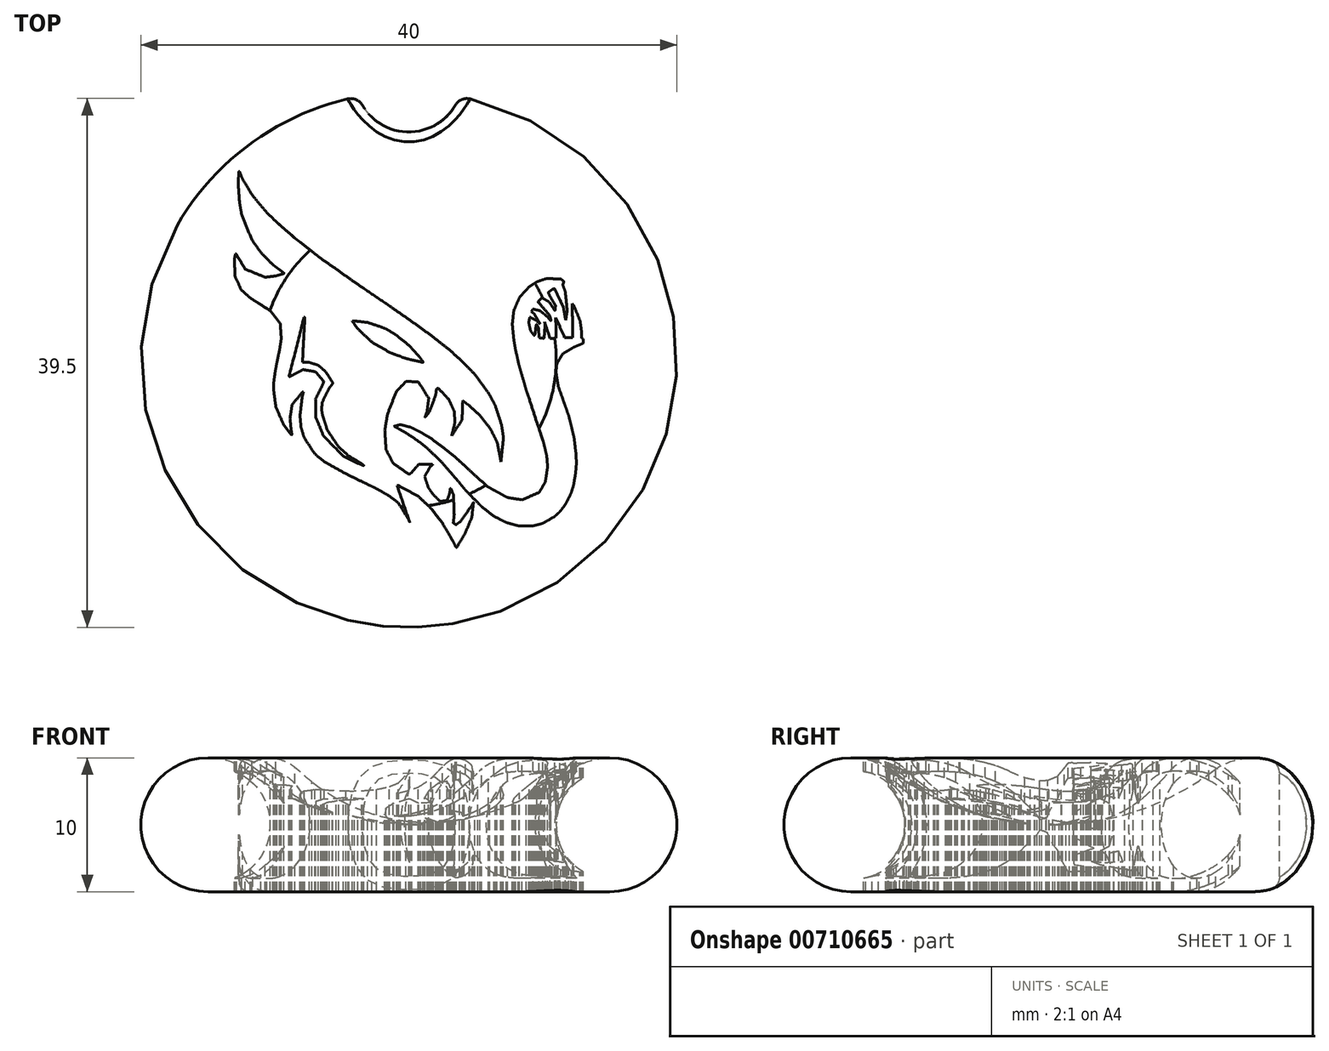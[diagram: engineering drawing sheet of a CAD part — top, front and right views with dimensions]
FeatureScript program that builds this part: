
annotation { "Feature Type Name" : "Feature", "Feature Type Description" : "" }
export const myFeature = defineFeature(function(context is Context, id is Id, definition is map)
    precondition{}
    {
        {
            var Q0;
            Q0=qCreatedBy(makeId("Front.planeOp"),FACE);
            var sketch = newSketch(context, id + "F0", { "sketchPlane" : qUnion([Q0])});
            skArc(sketch, "E0", {"start": v(-12, 9) * mm, "mid": v(-19.74, 6.58) * mm, "end": v(-15, 0) * mm});
            skLineSegment(sketch, "E1", {"start": v(0, 0) * mm, "end": v(-15, 0) * mm});
            skArc(sketch, "E2", {"start": v(-12, 9) * mm, "mid": v(-6.32, 6.03) * mm, "end": v(0, 5) * mm});
            skLineSegment(sketch, "E3", {"start": v(0, 0) * mm, "end": v(0, 5) * mm});
            skSolve(sketch);
        }
        {
            var Q0;
            Q0=makeQuery(id+"F0.imprint","IMPRINT",FACE,{"disambiguationData":[TD([[makeQuery(id+"F0.imprint","IMPRINT",EDGE,{"derivedFrom":sQuery(id+"F0.wireOp",EDGE,"E0")}),1.0]])]});
            var Q1;
            Q1=sQuery(id+"F0.wireOp",EDGE,"E3");
            revolve(context, id + "F1", {"surfaceOperationType" : NewSurfaceOperationType.NEW, "entities" : qUnion([Q0]), "axis" : qUnion([Q1]), "revolveType" : RevolveType.FULL});
        }
        {
            var Q0;
            Q0=qCreatedBy(makeId("Top.planeOp"),FACE);
            cPlane(context, id + "F2", {"entities" : qUnion([Q0]), "cplaneType" : CPlaneType.OFFSET, "offset" : 25 * mm, "width" : 150 * mm, "height" : 150 * mm});
        }
        {
            var Q0;
            Q0=qCreatedBy(id+"F2.planeOp",FACE);
            var sketch = newSketch(context, id + "F3", { "sketchPlane" : qUnion([Q0])});
            skLineSegment(sketch, "E4", {"start": v(0.07, -12.18) * mm, "end": v(-0.88, -9.42) * mm});
            skLineSegment(sketch, "E5", {"start": v(-0.88, -9.42) * mm, "end": v(-0.75, -9.42) * mm});
            skLineSegment(sketch, "E6", {"start": v(-0.75, -9.42) * mm, "end": v(0.69, -10.2) * mm});
            skLineSegment(sketch, "E7", {"start": v(0.69, -10.2) * mm, "end": v(1.64, -11.1) * mm});
            skLineSegment(sketch, "E8", {"start": v(1.64, -11.1) * mm, "end": v(2.5, -12.21) * mm});
            skLineSegment(sketch, "E9", {"start": v(2.5, -12.21) * mm, "end": v(3.22, -13.43) * mm});
            skLineSegment(sketch, "E10", {"start": v(3.22, -13.43) * mm, "end": v(3.46, -13.9) * mm});
            skLineSegment(sketch, "E11", {"start": v(3.46, -13.9) * mm, "end": v(3.55, -14.05) * mm});
            skLineSegment(sketch, "E12", {"start": v(3.55, -14.05) * mm, "end": v(4.21, -12.95) * mm});
            skLineSegment(sketch, "E13", {"start": v(4.21, -12.95) * mm, "end": v(4.7, -11.8) * mm});
            skLineSegment(sketch, "E14", {"start": v(4.7, -11.8) * mm, "end": v(4.82, -10.65) * mm});
            skLineSegment(sketch, "E15", {"start": v(4.82, -10.65) * mm, "end": v(4.73, -10.86) * mm});
            skLineSegment(sketch, "E16", {"start": v(4.73, -10.86) * mm, "end": v(3.84, -12.1) * mm});
            skLineSegment(sketch, "E17", {"start": v(3.84, -12.1) * mm, "end": v(3.52, -12.34) * mm});
            skLineSegment(sketch, "E18", {"start": v(3.52, -12.34) * mm, "end": v(3.31, -12.2) * mm});
            skLineSegment(sketch, "E19", {"start": v(3.31, -12.2) * mm, "end": v(3.39, -11.6) * mm});
            skLineSegment(sketch, "E20", {"start": v(3.39, -11.6) * mm, "end": v(3.33, -10.1) * mm});
            skLineSegment(sketch, "E21", {"start": v(3.33, -10.1) * mm, "end": v(3.14, -9.62) * mm});
            skLineSegment(sketch, "E22", {"start": v(3.14, -9.62) * mm, "end": v(3.1, -9.63) * mm});
            skLineSegment(sketch, "E23", {"start": v(3.1, -9.63) * mm, "end": v(3.03, -10.02) * mm});
            skLineSegment(sketch, "E24", {"start": v(3.03, -10.02) * mm, "end": v(2.86, -10.52) * mm});
            skLineSegment(sketch, "E25", {"start": v(2.86, -10.52) * mm, "end": v(2.33, -10.6) * mm});
            skLineSegment(sketch, "E26", {"start": v(2.33, -10.6) * mm, "end": v(1.78, -10.04) * mm});
            skLineSegment(sketch, "E27", {"start": v(1.78, -10.04) * mm, "end": v(1.45, -9.56) * mm});
            skLineSegment(sketch, "E28", {"start": v(1.45, -9.56) * mm, "end": v(1.18, -8.73) * mm});
            skLineSegment(sketch, "E29", {"start": v(1.18, -8.73) * mm, "end": v(1.63, -7.94) * mm});
            skLineSegment(sketch, "E30", {"start": v(1.63, -7.94) * mm, "end": v(1.79, -7.87) * mm});
            skLineSegment(sketch, "E31", {"start": v(1.79, -7.87) * mm, "end": v(1.68, -7.8) * mm});
            skLineSegment(sketch, "E32", {"start": v(1.68, -7.8) * mm, "end": v(0.73, -7.82) * mm});
            skLineSegment(sketch, "E33", {"start": v(0.73, -7.82) * mm, "end": v(0.17, -8.48) * mm});
            skLineSegment(sketch, "E34", {"start": v(0.17, -8.48) * mm, "end": v(0, -8.57) * mm});
            skLineSegment(sketch, "E35", {"start": v(0, -8.57) * mm, "end": v(-1.18, -7.73) * mm});
            skLineSegment(sketch, "E36", {"start": v(-1.18, -7.73) * mm, "end": v(-1.7, -6.73) * mm});
            skLineSegment(sketch, "E37", {"start": v(-1.7, -6.73) * mm, "end": v(-1.8, -5.27) * mm});
            skLineSegment(sketch, "E38", {"start": v(-1.8, -5.27) * mm, "end": v(-1.6, -4.06) * mm});
            skLineSegment(sketch, "E39", {"start": v(-1.6, -4.06) * mm, "end": v(-0.93, -2.38) * mm});
            skLineSegment(sketch, "E40", {"start": v(-0.93, -2.38) * mm, "end": v(-0.2, -1.64) * mm});
            skLineSegment(sketch, "E41", {"start": v(-0.2, -1.64) * mm, "end": v(0.7, -1.65) * mm});
            skLineSegment(sketch, "E42", {"start": v(0.7, -1.65) * mm, "end": v(1.48, -2.9) * mm});
            skLineSegment(sketch, "E43", {"start": v(1.48, -2.9) * mm, "end": v(1.36, -3.87) * mm});
            skLineSegment(sketch, "E44", {"start": v(1.36, -3.87) * mm, "end": v(1.2, -4.32) * mm});
            skLineSegment(sketch, "E45", {"start": v(1.2, -4.32) * mm, "end": v(1.55, -3.88) * mm});
            skLineSegment(sketch, "E46", {"start": v(1.55, -3.88) * mm, "end": v(2, -2.65) * mm});
            skLineSegment(sketch, "E47", {"start": v(2, -2.65) * mm, "end": v(2.07, -2.19) * mm});
            skLineSegment(sketch, "E48", {"start": v(2.07, -2.19) * mm, "end": v(2.2, -2.14) * mm});
            skLineSegment(sketch, "E49", {"start": v(2.2, -2.14) * mm, "end": v(2.97, -2.96) * mm});
            skLineSegment(sketch, "E50", {"start": v(2.97, -2.96) * mm, "end": v(3.39, -3.87) * mm});
            skLineSegment(sketch, "E51", {"start": v(3.39, -3.87) * mm, "end": v(3.44, -4.7) * mm});
            skLineSegment(sketch, "E52", {"start": v(3.44, -4.7) * mm, "end": v(3.22, -5.56) * mm});
            skLineSegment(sketch, "E53", {"start": v(3.22, -5.56) * mm, "end": v(3.2, -5.7) * mm});
            skLineSegment(sketch, "E54", {"start": v(3.2, -5.7) * mm, "end": v(3.97, -4.5) * mm});
            skLineSegment(sketch, "E55", {"start": v(3.97, -4.5) * mm, "end": v(4.02, -3.07) * mm});
            skLineSegment(sketch, "E56", {"start": v(4.02, -3.07) * mm, "end": v(4.5, -3.42) * mm});
            skLineSegment(sketch, "E57", {"start": v(4.5, -3.42) * mm, "end": v(5.3, -4.17) * mm});
            skLineSegment(sketch, "E58", {"start": v(5.3, -4.17) * mm, "end": v(6.05, -5.1) * mm});
            skLineSegment(sketch, "E59", {"start": v(6.05, -5.1) * mm, "end": v(6.59, -6.16) * mm});
            skLineSegment(sketch, "E60", {"start": v(6.59, -6.16) * mm, "end": v(6.85, -7.5) * mm});
            skLineSegment(sketch, "E61", {"start": v(6.85, -7.5) * mm, "end": v(6.87, -7.64) * mm});
            skLineSegment(sketch, "E62", {"start": v(6.87, -7.64) * mm, "end": v(7.06, -5.83) * mm});
            skLineSegment(sketch, "E63", {"start": v(7.06, -5.83) * mm, "end": v(6.91, -4.86) * mm});
            skLineSegment(sketch, "E64", {"start": v(6.91, -4.86) * mm, "end": v(6.45, -3.44) * mm});
            skLineSegment(sketch, "E65", {"start": v(6.45, -3.44) * mm, "end": v(5.94, -2.5) * mm});
            skLineSegment(sketch, "E66", {"start": v(5.94, -2.5) * mm, "end": v(4.93, -1.11) * mm});
            skLineSegment(sketch, "E67", {"start": v(4.93, -1.11) * mm, "end": v(3.78, 0.06) * mm});
            skLineSegment(sketch, "E68", {"start": v(3.78, 0.06) * mm, "end": v(2.93, 0.8) * mm});
            skLineSegment(sketch, "E69", {"start": v(2.93, 0.8) * mm, "end": v(1.83, 1.66) * mm});
            skLineSegment(sketch, "E70", {"start": v(1.83, 1.66) * mm, "end": v(0.88, 2.38) * mm});
            skLineSegment(sketch, "E71", {"start": v(0.88, 2.38) * mm, "end": v(-0.09, 3.06) * mm});
            skLineSegment(sketch, "E72", {"start": v(-0.09, 3.06) * mm, "end": v(-1.43, 4) * mm});
            skLineSegment(sketch, "E73", {"start": v(-1.43, 4) * mm, "end": v(-3.32, 5.28) * mm});
            skLineSegment(sketch, "E74", {"start": v(-3.32, 5.28) * mm, "end": v(-4.48, 6.08) * mm});
            skLineSegment(sketch, "E75", {"start": v(-4.48, 6.08) * mm, "end": v(-5.43, 6.77) * mm});
            skLineSegment(sketch, "E76", {"start": v(-5.43, 6.77) * mm, "end": v(-6.58, 7.57) * mm});
            skLineSegment(sketch, "E77", {"start": v(-6.58, 7.57) * mm, "end": v(-7.24, 8.07) * mm});
            skLineSegment(sketch, "E78", {"start": v(-7.24, 8.07) * mm, "end": v(-8.5, 9.07) * mm});
            skLineSegment(sketch, "E79", {"start": v(-8.5, 9.07) * mm, "end": v(-9.94, 10.33) * mm});
            skLineSegment(sketch, "E80", {"start": v(-9.94, 10.33) * mm, "end": v(-10.62, 11) * mm});
            skLineSegment(sketch, "E81", {"start": v(-10.62, 11) * mm, "end": v(-11.66, 12.24) * mm});
            skLineSegment(sketch, "E82", {"start": v(-11.66, 12.24) * mm, "end": v(-12.4, 13.46) * mm});
            skLineSegment(sketch, "E83", {"start": v(-12.4, 13.46) * mm, "end": v(-12.64, 14.05) * mm});
            skLineSegment(sketch, "E84", {"start": v(-12.64, 14.05) * mm, "end": v(-12.69, 14.05) * mm});
            skLineSegment(sketch, "E85", {"start": v(-12.69, 14.05) * mm, "end": v(-12.74, 13.18) * mm});
            skLineSegment(sketch, "E86", {"start": v(-12.74, 13.18) * mm, "end": v(-12.64, 11.7) * mm});
            skLineSegment(sketch, "E87", {"start": v(-12.64, 11.7) * mm, "end": v(-12.48, 10.82) * mm});
            skLineSegment(sketch, "E88", {"start": v(-12.48, 10.82) * mm, "end": v(-11.72, 8.95) * mm});
            skLineSegment(sketch, "E89", {"start": v(-11.72, 8.95) * mm, "end": v(-11.06, 8.01) * mm});
            skLineSegment(sketch, "E90", {"start": v(-11.06, 8.01) * mm, "end": v(-10.15, 7.08) * mm});
            skLineSegment(sketch, "E91", {"start": v(-10.15, 7.08) * mm, "end": v(-9.53, 6.62) * mm});
            skLineSegment(sketch, "E92", {"start": v(-9.53, 6.62) * mm, "end": v(-9.33, 6.47) * mm});
            skLineSegment(sketch, "E93", {"start": v(-9.33, 6.47) * mm, "end": v(-9.33, 6.42) * mm});
            skLineSegment(sketch, "E94", {"start": v(-9.33, 6.42) * mm, "end": v(-9.94, 6.25) * mm});
            skLineSegment(sketch, "E95", {"start": v(-9.94, 6.25) * mm, "end": v(-10.73, 6.15) * mm});
            skLineSegment(sketch, "E96", {"start": v(-10.73, 6.15) * mm, "end": v(-12.21, 6.75) * mm});
            skLineSegment(sketch, "E97", {"start": v(-12.21, 6.75) * mm, "end": v(-12.87, 7.83) * mm});
            skLineSegment(sketch, "E98", {"start": v(-12.87, 7.83) * mm, "end": v(-12.9, 7.88) * mm});
            skLineSegment(sketch, "E99", {"start": v(-12.9, 7.88) * mm, "end": v(-12.94, 7.9) * mm});
            skLineSegment(sketch, "E100", {"start": v(-12.94, 7.9) * mm, "end": v(-13.02, 7.52) * mm});
            skLineSegment(sketch, "E101", {"start": v(-13.02, 7.52) * mm, "end": v(-12.98, 6.24) * mm});
            skLineSegment(sketch, "E102", {"start": v(-12.98, 6.24) * mm, "end": v(-12.5, 5.2) * mm});
            skLineSegment(sketch, "E103", {"start": v(-12.5, 5.2) * mm, "end": v(-11.85, 4.61) * mm});
            skLineSegment(sketch, "E104", {"start": v(-11.85, 4.61) * mm, "end": v(-10.35, 3.65) * mm});
            skLineSegment(sketch, "E105", {"start": v(-10.35, 3.65) * mm, "end": v(-9.6, 2.71) * mm});
            skLineSegment(sketch, "E106", {"start": v(-9.6, 2.71) * mm, "end": v(-9.52, 1.56) * mm});
            skLineSegment(sketch, "E107", {"start": v(-9.52, 1.56) * mm, "end": v(-9.66, 0.71) * mm});
            skLineSegment(sketch, "E108", {"start": v(-9.66, 0.71) * mm, "end": v(-9.85, -0.2) * mm});
            skLineSegment(sketch, "E109", {"start": v(-9.85, -0.2) * mm, "end": v(-9.98, -0.93) * mm});
            skLineSegment(sketch, "E110", {"start": v(-9.98, -0.93) * mm, "end": v(-10.08, -1.62) * mm});
            skLineSegment(sketch, "E111", {"start": v(-10.08, -1.62) * mm, "end": v(-10.1, -2.3) * mm});
            skLineSegment(sketch, "E112", {"start": v(-10.1, -2.3) * mm, "end": v(-9.93, -3.55) * mm});
            skLineSegment(sketch, "E113", {"start": v(-9.93, -3.55) * mm, "end": v(-9.33, -4.9) * mm});
            skLineSegment(sketch, "E114", {"start": v(-9.33, -4.9) * mm, "end": v(-8.77, -5.62) * mm});
            skLineSegment(sketch, "E115", {"start": v(-8.77, -5.62) * mm, "end": v(-8.73, -5.6) * mm});
            skLineSegment(sketch, "E116", {"start": v(-8.73, -5.6) * mm, "end": v(-8.78, -5.33) * mm});
            skLineSegment(sketch, "E117", {"start": v(-8.78, -5.33) * mm, "end": v(-8.88, -4.41) * mm});
            skLineSegment(sketch, "E118", {"start": v(-8.88, -4.41) * mm, "end": v(-8.72, -3.39) * mm});
            skLineSegment(sketch, "E119", {"start": v(-8.72, -3.39) * mm, "end": v(-7.97, -2.44) * mm});
            skLineSegment(sketch, "E120", {"start": v(-7.97, -2.44) * mm, "end": v(-7.92, -2.41) * mm});
            skLineSegment(sketch, "E121", {"start": v(-7.92, -2.41) * mm, "end": v(-7.87, -2.41) * mm});
            skLineSegment(sketch, "E122", {"start": v(-7.87, -2.41) * mm, "end": v(-7.96, -2.8) * mm});
            skLineSegment(sketch, "E123", {"start": v(-7.96, -2.8) * mm, "end": v(-8.13, -4.2) * mm});
            skLineSegment(sketch, "E124", {"start": v(-8.13, -4.2) * mm, "end": v(-8.05, -5.05) * mm});
            skLineSegment(sketch, "E125", {"start": v(-8.05, -5.05) * mm, "end": v(-7.82, -5.83) * mm});
            skLineSegment(sketch, "E126", {"start": v(-7.82, -5.83) * mm, "end": v(-7.02, -7.05) * mm});
            skLineSegment(sketch, "E127", {"start": v(-7.02, -7.05) * mm, "end": v(-6.33, -7.62) * mm});
            skLineSegment(sketch, "E128", {"start": v(-6.33, -7.62) * mm, "end": v(-4.7, -8.54) * mm});
            skLineSegment(sketch, "E129", {"start": v(-4.7, -8.54) * mm, "end": v(-3.37, -9.19) * mm});
            skLineSegment(sketch, "E130", {"start": v(-3.37, -9.19) * mm, "end": v(-2.41, -9.64) * mm});
            skLineSegment(sketch, "E131", {"start": v(-2.41, -9.64) * mm, "end": v(-1.47, -10.19) * mm});
            skLineSegment(sketch, "E132", {"start": v(-1.47, -10.19) * mm, "end": v(-0.8, -10.7) * mm});
            skLineSegment(sketch, "E133", {"start": v(-0.8, -10.7) * mm, "end": v(0, -11.97) * mm});
            skLineSegment(sketch, "E134", {"start": v(0, -11.97) * mm, "end": v(0.07, -12.18) * mm});
            skLineSegment(sketch, "E135", {"start": v(-7.94, -0.21) * mm, "end": v(-7.42, -0.22) * mm});
            skLineSegment(sketch, "E136", {"start": v(-7.42, -0.22) * mm, "end": v(-6.76, -0.43) * mm});
            skLineSegment(sketch, "E137", {"start": v(-6.76, -0.43) * mm, "end": v(-6.2, -0.9) * mm});
            skLineSegment(sketch, "E138", {"start": v(-6.2, -0.9) * mm, "end": v(-5.68, -1.73) * mm});
            skLineSegment(sketch, "E139", {"start": v(-5.68, -1.73) * mm, "end": v(-5.7, -1.83) * mm});
            skLineSegment(sketch, "E140", {"start": v(-5.7, -1.83) * mm, "end": v(-5.95, -2.13) * mm});
            skLineSegment(sketch, "E141", {"start": v(-5.95, -2.13) * mm, "end": v(-6.46, -3.17) * mm});
            skLineSegment(sketch, "E142", {"start": v(-6.46, -3.17) * mm, "end": v(-6.52, -3.72) * mm});
            skLineSegment(sketch, "E143", {"start": v(-6.52, -3.72) * mm, "end": v(-6.43, -4.19) * mm});
            skLineSegment(sketch, "E144", {"start": v(-6.43, -4.19) * mm, "end": v(-6.08, -5.28) * mm});
            skLineSegment(sketch, "E145", {"start": v(-6.08, -5.28) * mm, "end": v(-5.24, -6.53) * mm});
            skLineSegment(sketch, "E146", {"start": v(-5.24, -6.53) * mm, "end": v(-4.53, -7.18) * mm});
            skLineSegment(sketch, "E147", {"start": v(-4.53, -7.18) * mm, "end": v(-3.52, -7.78) * mm});
            skLineSegment(sketch, "E148", {"start": v(-3.52, -7.78) * mm, "end": v(-3.35, -7.9) * mm});
            skLineSegment(sketch, "E149", {"start": v(-3.35, -7.9) * mm, "end": v(-3.41, -7.92) * mm});
            skLineSegment(sketch, "E150", {"start": v(-3.41, -7.92) * mm, "end": v(-4.9, -7.23) * mm});
            skLineSegment(sketch, "E151", {"start": v(-4.9, -7.23) * mm, "end": v(-6.38, -5.68) * mm});
            skLineSegment(sketch, "E152", {"start": v(-6.38, -5.68) * mm, "end": v(-6.94, -4.33) * mm});
            skLineSegment(sketch, "E153", {"start": v(-6.94, -4.33) * mm, "end": v(-6.97, -2.96) * mm});
            skLineSegment(sketch, "E154", {"start": v(-6.97, -2.96) * mm, "end": v(-6.4, -1.78) * mm});
            skLineSegment(sketch, "E155", {"start": v(-6.4, -1.78) * mm, "end": v(-6.36, -1.64) * mm});
            skLineSegment(sketch, "E156", {"start": v(-6.36, -1.64) * mm, "end": v(-6.97, -0.9) * mm});
            skLineSegment(sketch, "E157", {"start": v(-6.97, -0.9) * mm, "end": v(-7.9, -0.75) * mm});
            skLineSegment(sketch, "E158", {"start": v(-7.9, -0.75) * mm, "end": v(-8.75, -1.2) * mm});
            skLineSegment(sketch, "E159", {"start": v(-8.75, -1.2) * mm, "end": v(-8.9, -1.28) * mm});
            skLineSegment(sketch, "E160", {"start": v(-8.9, -1.28) * mm, "end": v(-8.94, -1.26) * mm});
            skLineSegment(sketch, "E161", {"start": v(-8.94, -1.26) * mm, "end": v(-7.83, 3.16) * mm});
            skLineSegment(sketch, "E162", {"start": v(-7.83, 3.16) * mm, "end": v(-7.77, 3.15) * mm});
            skLineSegment(sketch, "E163", {"start": v(-7.77, 3.15) * mm, "end": v(-7.94, -0.21) * mm});
            skLineSegment(sketch, "E164", {"start": v(-4.23, 2.88) * mm, "end": v(-4.07, 2.88) * mm});
            skLineSegment(sketch, "E165", {"start": v(-4.07, 2.88) * mm, "end": v(-3.07, 2.77) * mm});
            skLineSegment(sketch, "E166", {"start": v(-3.07, 2.77) * mm, "end": v(-1.78, 2.33) * mm});
            skLineSegment(sketch, "E167", {"start": v(-1.78, 2.33) * mm, "end": v(-0.94, 1.82) * mm});
            skLineSegment(sketch, "E168", {"start": v(-0.94, 1.82) * mm, "end": v(0.03, 1.04) * mm});
            skLineSegment(sketch, "E169", {"start": v(0.03, 1.04) * mm, "end": v(0.77, 0.23) * mm});
            skLineSegment(sketch, "E170", {"start": v(0.77, 0.23) * mm, "end": v(1.07, -0.2) * mm});
            skLineSegment(sketch, "E171", {"start": v(1.07, -0.2) * mm, "end": v(1.06, -0.22) * mm});
            skLineSegment(sketch, "E172", {"start": v(1.06, -0.22) * mm, "end": v(0.89, -0.18) * mm});
            skLineSegment(sketch, "E173", {"start": v(0.89, -0.18) * mm, "end": v(-0.23, 0.08) * mm});
            skLineSegment(sketch, "E174", {"start": v(-0.23, 0.08) * mm, "end": v(-1.43, 0.53) * mm});
            skLineSegment(sketch, "E175", {"start": v(-1.43, 0.53) * mm, "end": v(-2.76, 1.3) * mm});
            skLineSegment(sketch, "E176", {"start": v(-2.76, 1.3) * mm, "end": v(-3.82, 2.3) * mm});
            skLineSegment(sketch, "E177", {"start": v(-3.82, 2.3) * mm, "end": v(-4.23, 2.88) * mm});
            skLineSegment(sketch, "E178", {"start": v(10.06, 1.59) * mm, "end": v(9.72, 1.63) * mm});
            skLineSegment(sketch, "E179", {"start": v(9.35, 1.8) * mm, "end": v(9.08, 2.16) * mm});
            skLineSegment(sketch, "E180", {"start": v(9.08, 2.16) * mm, "end": v(8.95, 2.77) * mm});
            skLineSegment(sketch, "E181", {"start": v(8.95, 2.77) * mm, "end": v(9.03, 3.17) * mm});
            skLineSegment(sketch, "E182", {"start": v(9.15, 3.57) * mm, "end": v(9.25, 3.78) * mm});
            skLineSegment(sketch, "E183", {"start": v(9.64, 4.32) * mm, "end": v(9.93, 4.62) * mm});
            skLineSegment(sketch, "E184", {"start": v(10.38, 5) * mm, "end": v(10.7, 5.24) * mm});
            skLineSegment(sketch, "E185", {"start": v(10.7, 5.24) * mm, "end": v(10.87, 5.3) * mm});
            skLineSegment(sketch, "E186", {"start": v(11.5, 5.6) * mm, "end": v(11.5, 5.63) * mm});
            skLineSegment(sketch, "E187", {"start": v(11.5, 5.63) * mm, "end": v(11.57, 5.84) * mm});
            skLineSegment(sketch, "E188", {"start": v(11.57, 5.84) * mm, "end": v(11.33, 6.02) * mm});
            skLineSegment(sketch, "E189", {"start": v(11.33, 6.02) * mm, "end": v(10.26, 6.05) * mm});
            skLineSegment(sketch, "E190", {"start": v(10.26, 6.05) * mm, "end": v(9.55, 5.8) * mm});
            skLineSegment(sketch, "E191", {"start": v(9.55, 5.8) * mm, "end": v(8.99, 5.44) * mm});
            skLineSegment(sketch, "E192", {"start": v(8.99, 5.44) * mm, "end": v(8.26, 4.65) * mm});
            skLineSegment(sketch, "E193", {"start": v(8.26, 4.65) * mm, "end": v(7.83, 3.67) * mm});
            skLineSegment(sketch, "E194", {"start": v(7.83, 3.67) * mm, "end": v(7.72, 2.64) * mm});
            skLineSegment(sketch, "E195", {"start": v(7.72, 2.64) * mm, "end": v(7.82, 1.57) * mm});
            skLineSegment(sketch, "E196", {"start": v(7.82, 1.57) * mm, "end": v(7.96, 0.75) * mm});
            skLineSegment(sketch, "E197", {"start": v(7.96, 0.75) * mm, "end": v(8.22, -0.4) * mm});
            skLineSegment(sketch, "E198", {"start": v(8.22, -0.4) * mm, "end": v(8.51, -1.41) * mm});
            skLineSegment(sketch, "E199", {"start": v(8.51, -1.41) * mm, "end": v(8.77, -2.3) * mm});
            skLineSegment(sketch, "E200", {"start": v(8.77, -2.3) * mm, "end": v(8.95, -2.83) * mm});
            skLineSegment(sketch, "E201", {"start": v(8.95, -2.83) * mm, "end": v(9.55, -4.7) * mm});
            skLineSegment(sketch, "E202", {"start": v(9.55, -4.7) * mm, "end": v(10.03, -6.12) * mm});
            skLineSegment(sketch, "E203", {"start": v(10.03, -6.12) * mm, "end": v(10.3, -7.18) * mm});
            skLineSegment(sketch, "E204", {"start": v(10.3, -7.18) * mm, "end": v(10.36, -8.03) * mm});
            skLineSegment(sketch, "E205", {"start": v(10.36, -8.03) * mm, "end": v(10.18, -9.16) * mm});
            skLineSegment(sketch, "E206", {"start": v(10.18, -9.16) * mm, "end": v(9.73, -9.92) * mm});
            skLineSegment(sketch, "E207", {"start": v(9.73, -9.92) * mm, "end": v(8.46, -10.48) * mm});
            skLineSegment(sketch, "E208", {"start": v(8.46, -10.48) * mm, "end": v(7.35, -10.3) * mm});
            skLineSegment(sketch, "E209", {"start": v(7.35, -10.3) * mm, "end": v(5.93, -9.52) * mm});
            skLineSegment(sketch, "E210", {"start": v(5.93, -9.52) * mm, "end": v(5.13, -8.83) * mm});
            skLineSegment(sketch, "E211", {"start": v(5.13, -8.83) * mm, "end": v(4.04, -7.8) * mm});
            skLineSegment(sketch, "E212", {"start": v(4.04, -7.8) * mm, "end": v(3.4, -7.23) * mm});
            skLineSegment(sketch, "E213", {"start": v(3.4, -7.23) * mm, "end": v(2.59, -6.59) * mm});
            skLineSegment(sketch, "E214", {"start": v(2.59, -6.59) * mm, "end": v(1.57, -5.83) * mm});
            skLineSegment(sketch, "E215", {"start": v(1.57, -5.83) * mm, "end": v(0.83, -5.4) * mm});
            skLineSegment(sketch, "E216", {"start": v(0.83, -5.4) * mm, "end": v(0.12, -5.05) * mm});
            skLineSegment(sketch, "E217", {"start": v(0.12, -5.05) * mm, "end": v(-0.64, -4.85) * mm});
            skLineSegment(sketch, "E218", {"start": v(-0.64, -4.85) * mm, "end": v(-1.1, -4.99) * mm});
            skLineSegment(sketch, "E219", {"start": v(-1.1, -4.99) * mm, "end": v(-0.72, -5.18) * mm});
            skLineSegment(sketch, "E220", {"start": v(-0.72, -5.18) * mm, "end": v(0.22, -5.75) * mm});
            skLineSegment(sketch, "E221", {"start": v(0.22, -5.75) * mm, "end": v(0.85, -6.2) * mm});
            skLineSegment(sketch, "E222", {"start": v(0.85, -6.2) * mm, "end": v(1.45, -6.7) * mm});
            skLineSegment(sketch, "E223", {"start": v(1.45, -6.7) * mm, "end": v(2.43, -7.64) * mm});
            skLineSegment(sketch, "E224", {"start": v(2.43, -7.64) * mm, "end": v(3.27, -8.62) * mm});
            skLineSegment(sketch, "E225", {"start": v(3.27, -8.62) * mm, "end": v(3.76, -9.19) * mm});
            skLineSegment(sketch, "E226", {"start": v(3.76, -9.19) * mm, "end": v(4.11, -9.63) * mm});
            skLineSegment(sketch, "E227", {"start": v(4.11, -9.63) * mm, "end": v(4.54, -10.08) * mm});
            skLineSegment(sketch, "E228", {"start": v(4.54, -10.08) * mm, "end": v(5.44, -11) * mm});
            skLineSegment(sketch, "E229", {"start": v(5.44, -11) * mm, "end": v(6.34, -11.7) * mm});
            skLineSegment(sketch, "E230", {"start": v(6.34, -11.7) * mm, "end": v(7.27, -12.17) * mm});
            skLineSegment(sketch, "E231", {"start": v(7.27, -12.17) * mm, "end": v(8.15, -12.42) * mm});
            skLineSegment(sketch, "E232", {"start": v(8.15, -12.42) * mm, "end": v(9.26, -12.42) * mm});
            skLineSegment(sketch, "E233", {"start": v(9.26, -12.42) * mm, "end": v(10, -12.23) * mm});
            skLineSegment(sketch, "E234", {"start": v(10, -12.23) * mm, "end": v(10.88, -11.72) * mm});
            skLineSegment(sketch, "E235", {"start": v(10.88, -11.72) * mm, "end": v(11.29, -11.35) * mm});
            skLineSegment(sketch, "E236", {"start": v(11.29, -11.35) * mm, "end": v(11.68, -10.82) * mm});
            skLineSegment(sketch, "E237", {"start": v(11.68, -10.82) * mm, "end": v(12.1, -10.02) * mm});
            skLineSegment(sketch, "E238", {"start": v(12.1, -10.02) * mm, "end": v(12.3, -9.4) * mm});
            skLineSegment(sketch, "E239", {"start": v(12.3, -9.4) * mm, "end": v(12.45, -8.47) * mm});
            skLineSegment(sketch, "E240", {"start": v(12.45, -8.47) * mm, "end": v(12.51, -7.72) * mm});
            skLineSegment(sketch, "E241", {"start": v(12.51, -7.72) * mm, "end": v(12.46, -6.91) * mm});
            skLineSegment(sketch, "E242", {"start": v(12.46, -6.91) * mm, "end": v(12.45, -6.85) * mm});
            skLineSegment(sketch, "E243", {"start": v(12.45, -6.85) * mm, "end": v(12.33, -5.85) * mm});
            skLineSegment(sketch, "E244", {"start": v(12.33, -5.85) * mm, "end": v(12.13, -4.98) * mm});
            skLineSegment(sketch, "E245", {"start": v(12.13, -4.98) * mm, "end": v(11.94, -4.2) * mm});
            skLineSegment(sketch, "E246", {"start": v(11.94, -4.2) * mm, "end": v(11.66, -3.44) * mm});
            skLineSegment(sketch, "E247", {"start": v(11.66, -3.44) * mm, "end": v(11.16, -2.03) * mm});
            skLineSegment(sketch, "E248", {"start": v(11.16, -2.03) * mm, "end": v(10.98, -0.93) * mm});
            skLineSegment(sketch, "E249", {"start": v(10.98, -0.93) * mm, "end": v(11.04, -0.32) * mm});
            skLineSegment(sketch, "E250", {"start": v(11.04, -0.32) * mm, "end": v(11.48, 0.44) * mm});
            skLineSegment(sketch, "E251", {"start": v(11.48, 0.44) * mm, "end": v(12.32, 0.93) * mm});
            skLineSegment(sketch, "E252", {"start": v(12.32, 0.93) * mm, "end": v(13.02, 1.22) * mm});
            skLineSegment(sketch, "E253", {"start": v(13.02, 1.22) * mm, "end": v(13.02, 1.52) * mm});
            skLineSegment(sketch, "E254", {"start": v(13.02, 1.52) * mm, "end": v(12.9, 1.6) * mm});
            skLineSegment(sketch, "E255", {"start": v(12.22, 1.65) * mm, "end": v(11.63, 1.62) * mm});
            skLineSegment(sketch, "E256", {"start": v(10.98, 1.6) * mm, "end": v(10.54, 1.57) * mm});
            skLineSegment(sketch, "E257", {"start": v(12.9, 1.6) * mm, "end": v(12.88, 2.16) * mm});
            skLineSegment(sketch, "E258", {"start": v(12.88, 2.16) * mm, "end": v(12.78, 2.91) * mm});
            skLineSegment(sketch, "E259", {"start": v(12.78, 2.91) * mm, "end": v(12.3, 4.04) * mm});
            skLineSegment(sketch, "E260", {"start": v(12.3, 4.04) * mm, "end": v(12.2, 4.17) * mm});
            skLineSegment(sketch, "E261", {"start": v(12.2, 4.17) * mm, "end": v(12.22, 1.65) * mm});
            skLineSegment(sketch, "E262", {"start": v(10.87, 5.3) * mm, "end": v(11.52, 3.95) * mm});
            skLineSegment(sketch, "E263", {"start": v(11.52, 3.95) * mm, "end": v(11.7, 2.94) * mm});
            skLineSegment(sketch, "E264", {"start": v(11.7, 2.94) * mm, "end": v(11.82, 3.65) * mm});
            skLineSegment(sketch, "E265", {"start": v(11.82, 3.65) * mm, "end": v(11.68, 5.04) * mm});
            skLineSegment(sketch, "E266", {"start": v(11.68, 5.04) * mm, "end": v(11.5, 5.6) * mm});
            skLineSegment(sketch, "E267", {"start": v(11.63, 1.62) * mm, "end": v(10.97, 3.15) * mm});
            skLineSegment(sketch, "E268", {"start": v(10.97, 3.15) * mm, "end": v(10.98, 1.6) * mm});
            skLineSegment(sketch, "E269", {"start": v(9.25, 3.78) * mm, "end": v(9.8, 3.64) * mm});
            skLineSegment(sketch, "E270", {"start": v(9.8, 3.64) * mm, "end": v(10.34, 3.2) * mm});
            skLineSegment(sketch, "E271", {"start": v(10.34, 3.2) * mm, "end": v(10.58, 2.91) * mm});
            skLineSegment(sketch, "E272", {"start": v(10.58, 2.91) * mm, "end": v(10.61, 2.92) * mm});
            skLineSegment(sketch, "E273", {"start": v(10.61, 2.92) * mm, "end": v(10.52, 3.29) * mm});
            skLineSegment(sketch, "E274", {"start": v(10.52, 3.29) * mm, "end": v(9.66, 4.3) * mm});
            skLineSegment(sketch, "E275", {"start": v(9.66, 4.3) * mm, "end": v(9.64, 4.32) * mm});
            skLineSegment(sketch, "E276", {"start": v(9.93, 4.62) * mm, "end": v(10.47, 4.3) * mm});
            skLineSegment(sketch, "E277", {"start": v(10.47, 4.3) * mm, "end": v(10.87, 3.7) * mm});
            skLineSegment(sketch, "E278", {"start": v(10.87, 3.7) * mm, "end": v(10.9, 3.63) * mm});
            skLineSegment(sketch, "E279", {"start": v(10.9, 3.63) * mm, "end": v(10.95, 4.02) * mm});
            skLineSegment(sketch, "E280", {"start": v(10.95, 4.02) * mm, "end": v(10.38, 5) * mm});
            skLineSegment(sketch, "E281", {"start": v(10.54, 1.57) * mm, "end": v(10.13, 2.8) * mm});
            skLineSegment(sketch, "E282", {"start": v(10.13, 2.8) * mm, "end": v(10.17, 2.58) * mm});
            skLineSegment(sketch, "E283", {"start": v(10.17, 2.58) * mm, "end": v(10.1, 1.65) * mm});
            skLineSegment(sketch, "E284", {"start": v(10.1, 1.65) * mm, "end": v(10.06, 1.59) * mm});
            skLineSegment(sketch, "E285", {"start": v(9.03, 3.17) * mm, "end": v(9.55, 2.9) * mm});
            skLineSegment(sketch, "E286", {"start": v(9.55, 2.9) * mm, "end": v(9.8, 2.66) * mm});
            skLineSegment(sketch, "E287", {"start": v(9.8, 2.66) * mm, "end": v(9.34, 3.45) * mm});
            skLineSegment(sketch, "E288", {"start": v(9.34, 3.45) * mm, "end": v(9.15, 3.57) * mm});
            skLineSegment(sketch, "E289", {"start": v(9.72, 1.63) * mm, "end": v(9.68, 2.35) * mm});
            skLineSegment(sketch, "E290", {"start": v(9.68, 2.35) * mm, "end": v(9.54, 2.65) * mm});
            skLineSegment(sketch, "E291", {"start": v(9.5, 2.54) * mm, "end": v(9.41, 1.87) * mm});
            skLineSegment(sketch, "E292", {"start": v(9.41, 1.87) * mm, "end": v(9.35, 1.8) * mm});
            skLineSegment(sketch, "E293", {"start": v(9.5, 2.54) * mm, "end": v(9.54, 2.65) * mm});
            skSolve(sketch);
        }
        {
            var Q0;
            Q0=makeQuery(id+"F3.imprint","IMPRINT",FACE,{"disambiguationData":[TD([[makeQuery(id+"F3.imprint","IMPRINT",EDGE,{"derivedFrom":sQuery(id+"F3.wireOp",EDGE,"E4")}),1.0]])]});
            var Q1;
            Q1=makeQuery(id+"F3.imprint","IMPRINT",FACE,{"disambiguationData":[TD([[makeQuery(id+"F3.imprint","IMPRINT",EDGE,{"derivedFrom":sQuery(id+"F3.wireOp",EDGE,"E178")}),1.0]])]});
            extrude(context, id + "F4", {"entities" : qUnion([Q0, Q1]), "operationType" : NewBodyOperationType.REMOVE, "oppositeDirection" : true, "depth" : 100 * mm, "offsetDistance" : 25 * mm});
        }
        {
            var Q0;
            Q0=qCreatedBy(makeId("Front.planeOp"),FACE);
            var sketch = newSketch(context, id + "F5", { "sketchPlane" : qUnion([Q0])});
            skCircle(sketch, "E294", {"center": v(-15, 5) * mm, "radius": 4 * mm});
            skSolve(sketch);
        }
        {
            var Q0;
            Q0 = qSketchRegion(id + "F5", true);
            var Q1;
            Q1=sQuery(id+"F0.wireOp",EDGE,"E3");
            revolve(context, id + "F6", {"operationType" : NewBodyOperationType.ADD, "surfaceOperationType" : NewSurfaceOperationType.NEW, "entities" : qUnion([Q0]), "axis" : qUnion([Q1]), "revolveType" : RevolveType.FULL});
        }
        {
            var Q0;
            Q0=qCreatedBy(id+"F2.planeOp",FACE);
            var sketch = newSketch(context, id + "F7", { "sketchPlane" : qUnion([Q0])});
            skCircle(sketch, "E295", {"center": v(0, 21) * mm, "radius": 4 * mm});
            skSolve(sketch);
        }
        {
            var Q0;
            Q0=makeQuery(id+"F7.imprint","IMPRINT",FACE,{"disambiguationData":[TD([[makeQuery(id+"F7.imprint","IMPRINT",EDGE,{"derivedFrom":sQuery(id+"F7.wireOp",EDGE,"E295")}),1.0]])]});
            extrude(context, id + "F8", {"entities" : qUnion([Q0]), "operationType" : NewBodyOperationType.REMOVE, "oppositeDirection" : true, "depth" : 30 * mm, "offsetDistance" : 25 * mm});
        }
        {
            var Q0;
            Q0=makeQuery(id+"F8.boolean.opBoolean","INTERSECT",EDGE,{"derivedFrom":[makeQuery(id+"F4.boolean.opBoolean","SPLIT",FACE,{"disambiguationData":[TD([makeQuery(id+"F1.opRevolve","SWEPT_FACE",FACE,{"disambiguationData":[OSD([sQuery(id+"F0.wireOp",EDGE,"E1")])]})])],"derivedFrom":makeQuery(id+"F1.opRevolve","SWEPT_FACE",FACE,{"disambiguationData":[OSD([sQuery(id+"F0.wireOp",EDGE,"E0")])]})}),makeQuery(id+"F8.opExtrude","SWEPT_FACE",FACE,{"disambiguationData":[OSD([sQuery(id+"F7.wireOp",EDGE,"E295")])]})]});
            fillet(context, id + "F9", {"entities" : qUnion([Q0]), "radius" : 1 * mm, "tangentPropagation" : true, "allowEdgeOverflow" : false});
        }
    });
